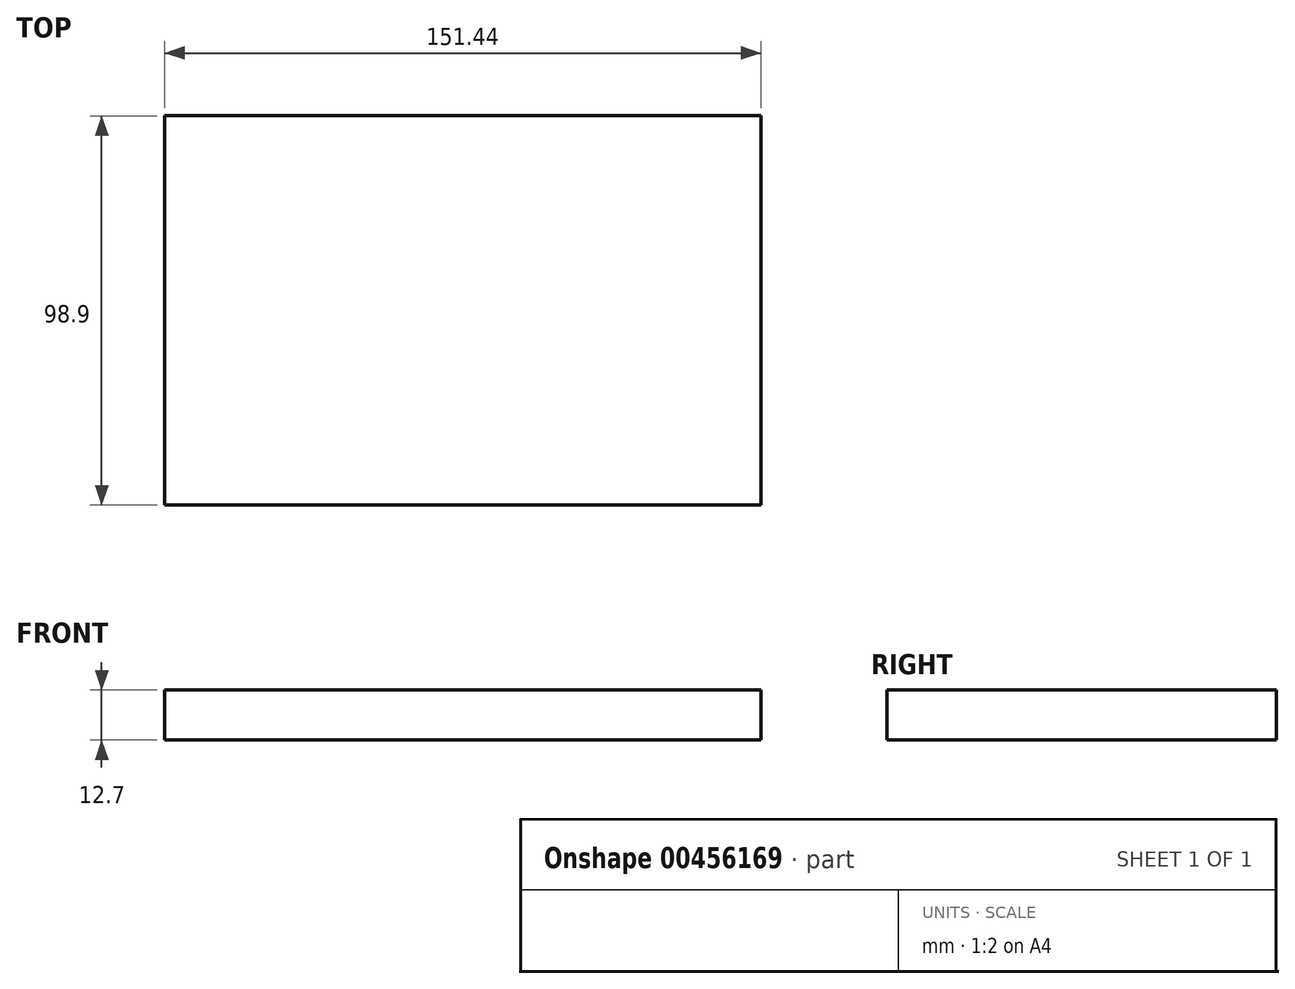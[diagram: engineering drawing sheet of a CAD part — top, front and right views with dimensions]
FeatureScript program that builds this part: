
annotation { "Feature Type Name" : "Feature", "Feature Type Description" : "" }
export const myFeature = defineFeature(function(context is Context, id is Id, definition is map)
    precondition{}
    {
        {
            var Q0;
            Q0=qCreatedBy(makeId("Top.planeOp"),FACE);
            var sketch = newSketch(context, id + "F0", { "sketchPlane" : qUnion([Q0])});
            skLineSegment(sketch, "E0.bottom", {"start": v(-76.06, -23.58) * mm, "end": v(75.38, -23.58) * mm});
            skLineSegment(sketch, "E0.top", {"start": v(-76.06, 75.32) * mm, "end": v(75.38, 75.32) * mm});
            skLineSegment(sketch, "E0.left", {"start": v(-76.06, -23.58) * mm, "end": v(-76.06, 75.32) * mm});
            skLineSegment(sketch, "E0.right", {"start": v(75.38, -23.58) * mm, "end": v(75.38, 75.32) * mm});
            skSolve(sketch);
        }
        {
            var Q0;
            Q0 = qSketchRegion(id + "F0", true);
            extrude(context, id + "F1", {"entities" : qUnion([Q0]), "depth" : 12.7 * mm});
        }
    });
